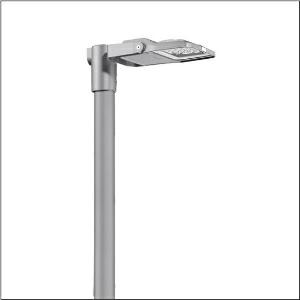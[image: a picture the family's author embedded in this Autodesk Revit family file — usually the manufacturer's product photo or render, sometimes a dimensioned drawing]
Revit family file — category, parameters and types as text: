
# Revit family: floodlight_fl_21_iq_micro___pl43_5xa7762a2a3a_62d6
name_source: partatom
category: Lighting Fixtures
units: mm (PartAtom-declared; Revit-internal decimal feet)

## family parameters
Cut with Voids When Loaded = No
Host = Face
Light Source = No
Part Type = Normal
Room Calculation Point = No
Round Connector Dimension = Use Diameter
Shared = No

## types (1)
- --- (1 x LED, 3040 lm, 23.1 W, 3000K)
    Apparent Load = 23 VA
    CIE Flux Codes = 29 80 99 100 100
    Color Rendering = 70
    Color Temperature = 3000K
    Default Elevation = 1800 mm
    Description = Floodlight FL 21 iQ micro, floodlight, primary light control with lens, of PMMA, primary optical cover: protective disc, of toughened safety glass, transparent, light distribution: PL43, light emission: direct distribution, installation type: surface-mounted, LED, High Power LED, rated luminous flux: 3.040lm, luminous efficacy: 132lm/W, light colour: 730, colour temperature: 3000K, control: Auto-Match, Temp-Guard, Night-Set, Smart-Wire, Desk-Remote (wireless, voltage-free reading and setting of iQ features in the workshop via application-optimized NFC function/RFID function), optimised constant luminous flux control (CLO 2.0), Street-Remote, with terminal, 6-pole, mains connection: 220..240V, AC, 50/60Hz, start of lifetime: 23W, end of service life: 24W, reduction: 11W, luminaire housing, of diecast aluminium, powder-coated, Siteco® metallic grey (DB 702S), corrosivity category C5 mid according to DIN EN ISO 12944, sealing non-destructively replaceable, please order mast flange separately, mast bracket, of steel, galvanised, powder-coated, Siteco® metallic grey (DB 702S), protection rating (complete): IP66, insulation class (complete): insulation class II (safety insulation), certification: CE, ENEC, VDE, protection symbol: D, impact resistance: IK07, permissible operating ambient temperature: -40..+40°C, permissible operating ambient temperature for outdoor applications: -40..+50°C, standard: DIN EN 12944, LABS conformity tested according to VDMA 24364:2018-05, packaging unit: 1 piece

Light Distribution: PL43
    Height = 65 mm
    Lamp = 1 x LED
    Lamp Light Flux = 3040 lm
    Lamp Power = 23.1 W
    Lamp count = 1
    Length = 312 mm
    Luminous efficacy = 132 lm/W
    Manufacturer = Siteco
    ModVariant = No
    Model = 5XA7762A2A3A
    Number of Poles = 1
    OnlyDefault = Yes
    Power Factor = 1
    Product Name = Floodlight FL 21 iQ micro | PL43
    Product group = floodlight | pylon annexe
    ProductGroupID = 6200
    Protection Class = Protection class II
    Protection Degree = IP 66
    RLX_Detail_Level = 1
    RLX_Emergency_Light_Flux = 0 lm
    RLX_Emergency_Type = 0
    RLX_Emergency_Type_DB = No
    RlxData = <blob elided: 101745 chars, md5=07680bce>
    Socket = socket
    Standby Power = 0 W
    System Light Flux = 3040 lm
    System Power = 23 W
    Type Comments = factory setting: luminous flux: 100 % | dim-lin: 254 | 455 mA
    Type Image = l_1007121.jpg
    URL = http://relux.com
    VarID = @adj_127739
    Voltage = 0 V
    Weight = 0.00 kg
    Width = 230 mm

## geometry (parser evidence)
native form markers: Blend x4, Sweep x12
no freeform markers — native parametric forms only
